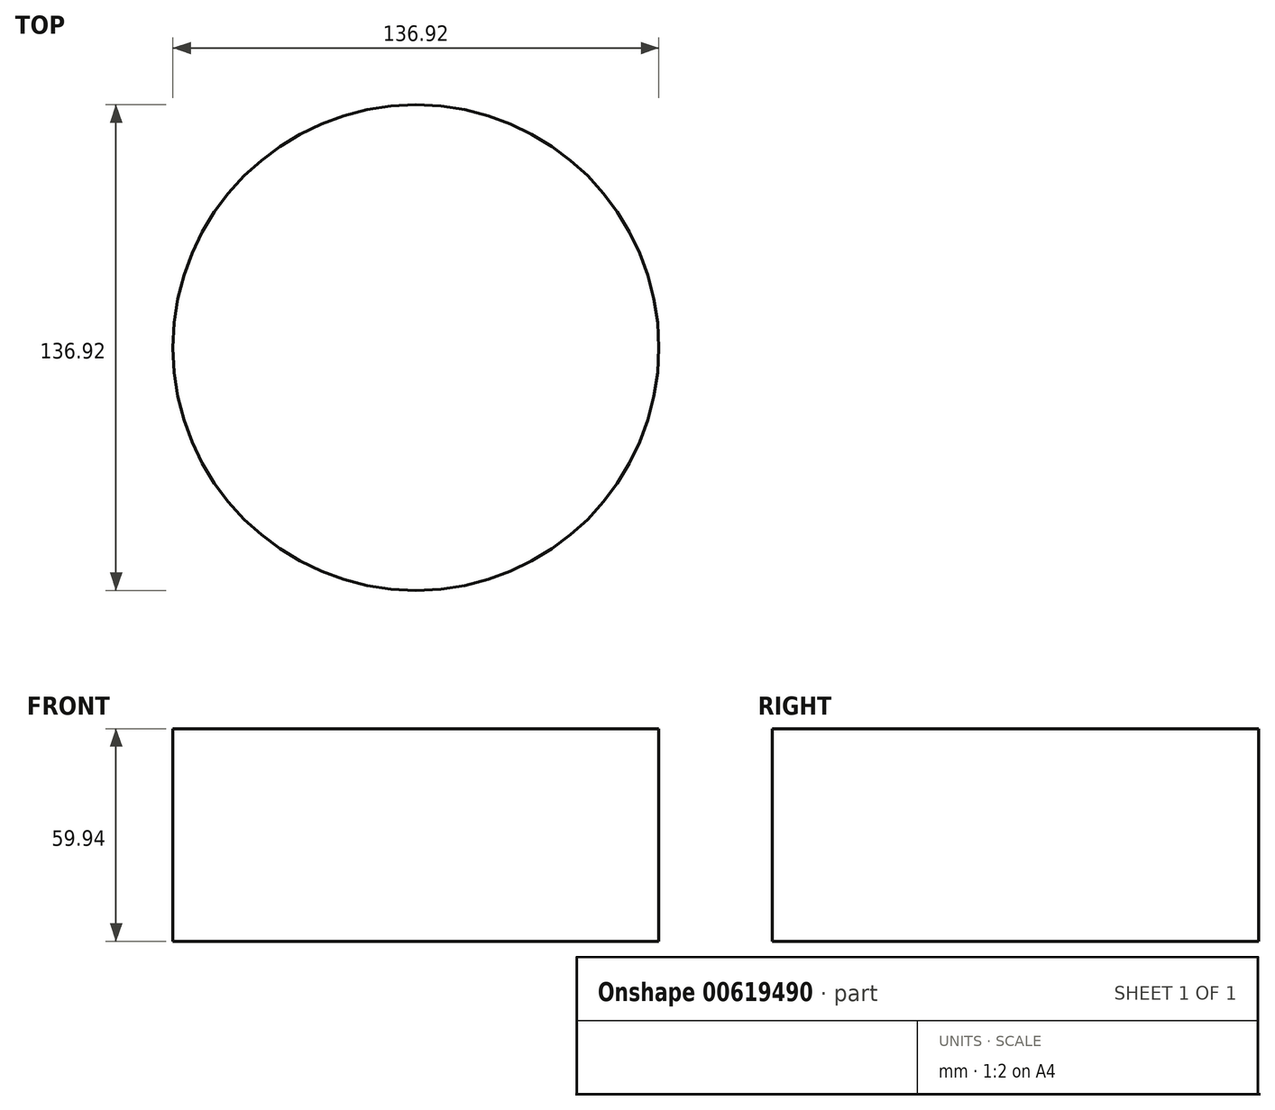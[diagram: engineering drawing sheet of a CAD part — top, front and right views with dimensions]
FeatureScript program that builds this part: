
annotation { "Feature Type Name" : "Feature", "Feature Type Description" : "" }
export const myFeature = defineFeature(function(context is Context, id is Id, definition is map)
    precondition{}
    {
        {
            var Q0;
            Q0=qCreatedBy(makeId("Top.planeOp"),FACE);
            var sketch = newSketch(context, id + "F0", { "sketchPlane" : qUnion([Q0])});
            skCircle(sketch, "E0", {"center": v(0, 0) * mm, "radius": 68.46 * mm});
            skSolve(sketch);
        }
        {
            var Q0;
            Q0=makeQuery(id+"F0.imprint","IMPRINT",FACE,{"disambiguationData":[TD([[makeQuery(id+"F0.imprint","IMPRINT",EDGE,{"derivedFrom":sQuery(id+"F0.wireOp",EDGE,"E0")}),1.0]])]});
            extrude(context, id + "F1", {"entities" : qUnion([Q0]), "depth" : 59.94 * mm, "offsetDistance" : 25.4 * mm});
        }
    });
